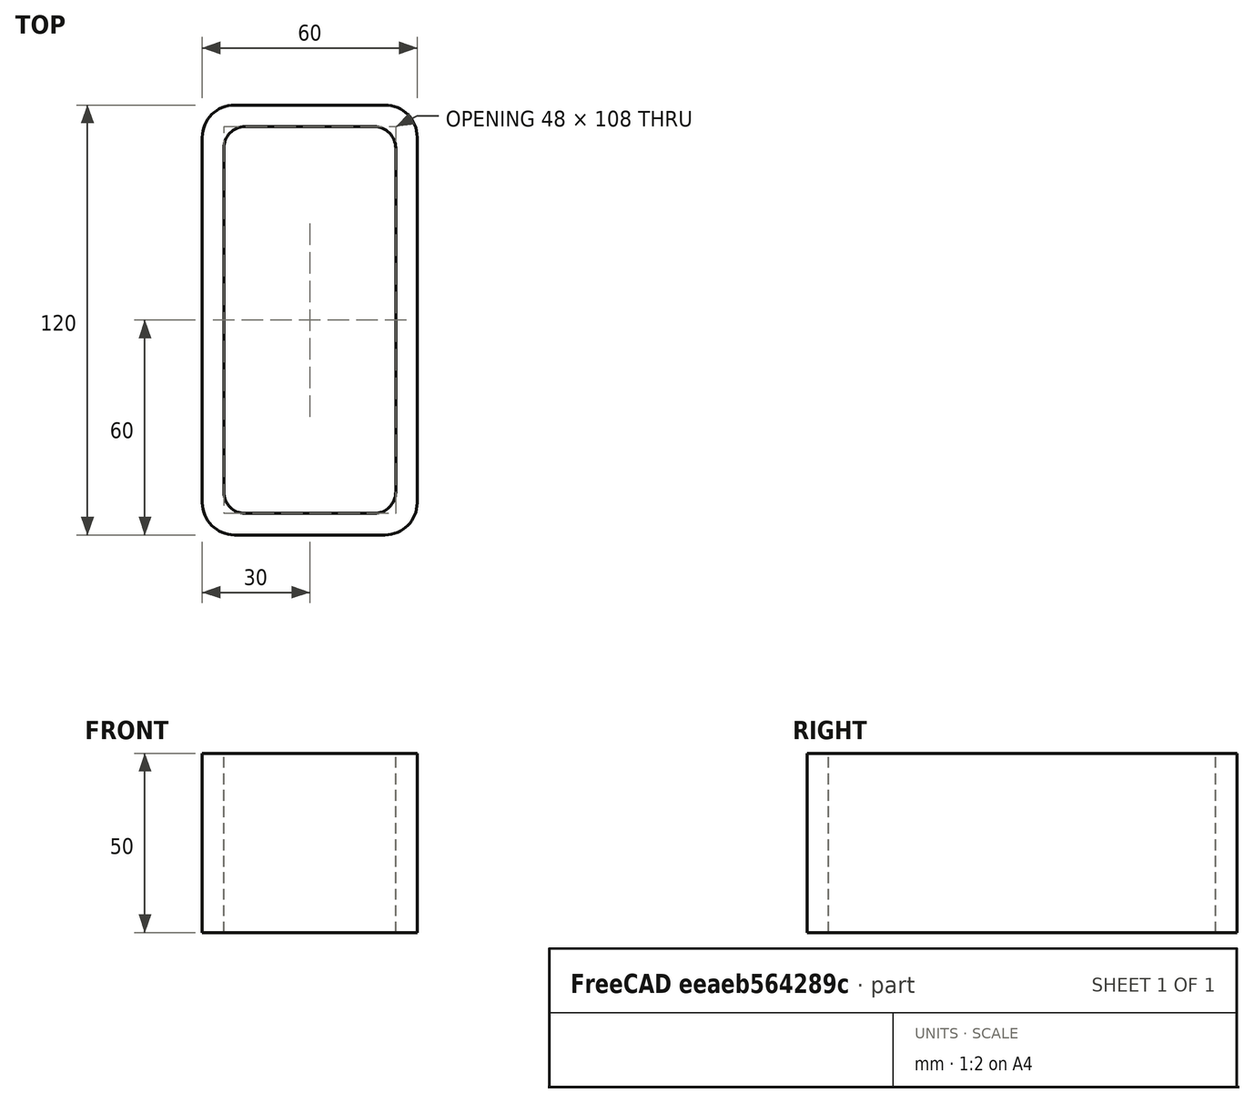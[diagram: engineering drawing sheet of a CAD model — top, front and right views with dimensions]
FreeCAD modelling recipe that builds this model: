
FCSTD DOCUMENT  (FreeCAD 0.15R4671 (Git))
Label: Rectangular hollow section 120x60x6 EN10219 S235JRH
License: All rights reserved
LicenseURL: http://en.wikipedia.org/wiki/All_rights_reserved
objects: Sketcher::SketchObject×1, Part::Extrusion×1
note: 2 computed .brp shape members not serialized (recipe doc carries the construction recipe); baked Part::Feature solids carry a one-line shape summary decoded from their .brp

FEATURE [Sketcher::SketchObject] Sketch
  sketch-geometry (16):
    g0: LineSegment StartX=-18 StartY=54 StartZ=0 EndX=18 EndY=54 EndZ=0
    g1: LineSegment StartX=24 StartY=48 StartZ=0 EndX=24 EndY=-48 EndZ=0
    g2: LineSegment StartX=18 StartY=-54 StartZ=0 EndX=-18 EndY=-54 EndZ=0
    g3: LineSegment StartX=-24 StartY=-48 StartZ=0 EndX=-24 EndY=48 EndZ=0
    g4: LineSegment StartX=-21 StartY=60 StartZ=0 EndX=21 EndY=60 EndZ=0
    g5: LineSegment StartX=30 StartY=51 StartZ=0 EndX=30 EndY=-51 EndZ=0
    g6: LineSegment StartX=21 StartY=-60 StartZ=0 EndX=-21 EndY=-60 EndZ=0
    g7: LineSegment StartX=-30 StartY=-51 StartZ=0 EndX=-30 EndY=51 EndZ=0
    g8: ArcOfCircle CenterX=-18 CenterY=48 CenterZ=0 NormalX=0 NormalY=0 NormalZ=1 Radius=6 StartAngle=1.5708 EndAngle=3.14159
    g9: ArcOfCircle CenterX=18 CenterY=48 CenterZ=0 NormalX=0 NormalY=0 NormalZ=1 Radius=6 StartAngle=0 EndAngle=1.5708
    g10: ArcOfCircle CenterX=18 CenterY=-48 CenterZ=0 NormalX=0 NormalY=0 NormalZ=1 Radius=6 StartAngle=4.71239 EndAngle=6.28319
    g11: ArcOfCircle CenterX=-18 CenterY=-48 CenterZ=0 NormalX=0 NormalY=0 NormalZ=1 Radius=6 StartAngle=3.14159 EndAngle=4.71239
    g12: ArcOfCircle CenterX=21 CenterY=51 CenterZ=0 NormalX=0 NormalY=0 NormalZ=1 Radius=9 StartAngle=0 EndAngle=1.5708
    g13: ArcOfCircle CenterX=21 CenterY=-51 CenterZ=0 NormalX=0 NormalY=0 NormalZ=1 Radius=9 StartAngle=4.71239 EndAngle=6.28319
    g14: ArcOfCircle CenterX=-21 CenterY=-51 CenterZ=0 NormalX=0 NormalY=0 NormalZ=1 Radius=9 StartAngle=3.14159 EndAngle=4.71239
    g15: ArcOfCircle CenterX=-21 CenterY=51 CenterZ=0 NormalX=0 NormalY=0 NormalZ=1 Radius=9 StartAngle=1.5708 EndAngle=3.14159
  constraints (36):
    c: Horizontal(g2)
    c: Vertical(g3)
    c: Horizontal(g6)
    c: Vertical(g7)
    c: Tangent(g3,g8) = 1.5708
    c: Tangent(g0,g8) = 1.5708
    c: Tangent(g0,g9) = 1.5708
    c: Tangent(g1,g9) = 1.5708
    c: Tangent(g1,g10) = 1.5708
    c: Tangent(g2,g10) = 1.5708
    c: Tangent(g2,g11) = 1.5708
    c: Tangent(g3,g11) = 1.5708
    c: Tangent(g4,g12) = 1.5708
    c: Tangent(g5,g12) = 1.5708
    c: Tangent(g5,g13) = 1.5708
    c: Tangent(g6,g13) = 1.5708
    c: Tangent(g6,g14) = 1.5708
    c: Tangent(g7,g14) = 1.5708
    c: Tangent(g7,g15) = 1.5708
    c: Tangent(g4,g15) = 1.5708
    c: Equal(g9,g8)
    c: Equal(g9,g11)
    c: Equal(g9,g10)
    c: Equal(g12,g15)
    c: Equal(g12,g14)
    c: Equal(g12,g13)
    c: Symmetric(g4,g6,g-1)
    c: Symmetric(g7,g5,g-2)
    c: DistanceY(g4,g6) = -120
    c: DistanceX(g7,g5) = 60
    c: Symmetric(g3,g1,g-2)
    c: Symmetric(g0,g2,g-1)
    c: DistanceY(g0,g4) = 6
    c: DistanceX(g5,g1) = -6
    c: Radius(g9) = 6
    c: Radius(g12) = 9
FEATURE [Part::Extrusion] Extrude  label="Rectangular hollow section 120x60x6 EN10219 S235JRH"
  Base = -> Sketch
  Dir = (0,0,50)
  Solid = true
